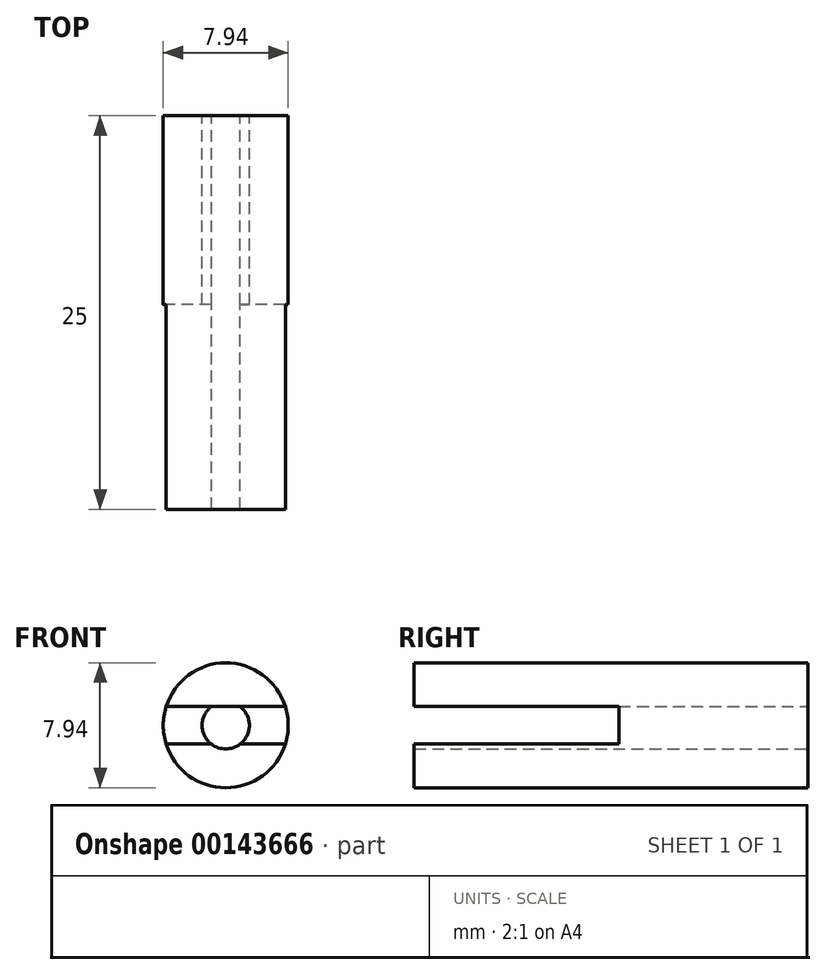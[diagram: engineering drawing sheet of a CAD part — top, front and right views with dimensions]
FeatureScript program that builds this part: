
annotation { "Feature Type Name" : "Feature", "Feature Type Description" : "" }
export const myFeature = defineFeature(function(context is Context, id is Id, definition is map)
    precondition{}
    {
        {
            var Q0;
            Q0=qCreatedBy(makeId("Front.planeOp"),FACE);
            var sketch = newSketch(context, id + "F0", { "sketchPlane" : qUnion([Q0])});
            skCircle(sketch, "E0", {"center": v(-45.73, 22.68) * mm, "radius": 3.97 * mm});
            skLineSegment(sketch, "E1", {"start": v(-41.94, 21.49) * mm, "end": v(-49.51, 21.49) * mm});
            skCircle(sketch, "E2", {"center": v(-45.73, 22.68) * mm, "radius": 1.5 * mm});
            skLineSegment(sketch, "E3", {"start": v(-41.94, 23.87) * mm, "end": v(-49.51, 23.87) * mm});
            skSolve(sketch);
        }
        {
            var Q0;
            Q0=makeQuery(id+"F0.imprint","IMPRINT",FACE,{"disambiguationData":[TD([[makeQuery(id+"F0.imprint","IMPRINT",EDGE,{"derivedFrom":sQuery(id+"F0.wireOp",EDGE,"Usm6nLvA-fHHg-3Ia8-UZyx-qVzBW3ukUWrC.bottom")}),-1.0]])]});
            var Q1;
            {var subQ0=sQuery(id+"F0.wireOp",EDGE,"E1");var subQ1=sQuery(id+"F0.wireOp",EDGE,"E0");var subQ2=makeQuery(id+"F0.imprint","INTERSECT",VERTEX,{"disambiguationData":[OD(0.0)],"derivedFrom":[subQ1,subQ0]});Q1=makeQuery(id+"F0.imprint","IMPRINT",FACE,{"disambiguationData":[TD([[makeQuery(id+"F0.imprint","IMPRINT",EDGE,{"disambiguationData":[TD([[subQ2,1.0]])],"derivedFrom":subQ1}),1.0]])]});}
            var Q2;
            {var subQ0=sQuery(id+"F0.wireOp",EDGE,"E2");var subQ1=sQuery(id+"F0.wireOp",EDGE,"E1");var subQ2=makeQuery(id+"F0.imprint","INTERSECT",VERTEX,{"disambiguationData":[OD(0.0)],"derivedFrom":[subQ1,subQ0]});Q2=makeQuery(id+"F0.imprint","IMPRINT",FACE,{"disambiguationData":[TD([[makeQuery(id+"F0.imprint","IMPRINT",EDGE,{"disambiguationData":[TD([[subQ2,-1.0]])],"derivedFrom":subQ1}),1.0]])]});}
            var Q3;
            {var subQ0=sQuery(id+"F0.wireOp",EDGE,"E3");var subQ1=sQuery(id+"F0.wireOp",EDGE,"E2");var subQ2=makeQuery(id+"F0.imprint","INTERSECT",VERTEX,{"disambiguationData":[OD(0.0)],"derivedFrom":[subQ1,subQ0]});Q3=makeQuery(id+"F0.imprint","IMPRINT",FACE,{"disambiguationData":[TD([[makeQuery(id+"F0.imprint","IMPRINT",EDGE,{"disambiguationData":[TD([[subQ2,1.0]])],"derivedFrom":subQ1}),1.0]])]});}
            var Q4;
            {var subQ0=sQuery(id+"F0.wireOp",EDGE,"E3");var subQ1=sQuery(id+"F0.wireOp",EDGE,"E0");var subQ2=makeQuery(id+"F0.imprint","INTERSECT",VERTEX,{"disambiguationData":[OD(0.0)],"derivedFrom":[subQ1,subQ0]});Q4=makeQuery(id+"F0.imprint","IMPRINT",FACE,{"disambiguationData":[TD([[makeQuery(id+"F0.imprint","IMPRINT",EDGE,{"disambiguationData":[TD([[subQ2,-1.0]])],"derivedFrom":subQ1}),1.0]])]});}
            extrude(context, id + "F1", {"entities" : qUnion([Q0, Q1, Q2, Q3, Q4]), "depth" : 25 * mm});
        }
        {
            var Q0;
            {var subQ0=sQuery(id+"F0.wireOp",EDGE,"E1");var subQ1=sQuery(id+"F0.wireOp",EDGE,"E0");var subQ2=makeQuery(id+"F0.imprint","INTERSECT",VERTEX,{"disambiguationData":[OD(1.0)],"derivedFrom":[subQ1,subQ0]});Q0=makeQuery(id+"F0.imprint","IMPRINT",FACE,{"disambiguationData":[TD([[makeQuery(id+"F0.imprint","IMPRINT",EDGE,{"disambiguationData":[TD([[subQ2,1.0]])],"derivedFrom":subQ1}),1.0]])]});}
            var Q1;
            {var subQ0=sQuery(id+"F0.wireOp",EDGE,"E1");var subQ1=sQuery(id+"F0.wireOp",EDGE,"E0");var subQ2=makeQuery(id+"F0.imprint","INTERSECT",VERTEX,{"disambiguationData":[OD(0.0)],"derivedFrom":[subQ1,subQ0]});Q1=makeQuery(id+"F0.imprint","IMPRINT",FACE,{"disambiguationData":[TD([[makeQuery(id+"F0.imprint","IMPRINT",EDGE,{"disambiguationData":[TD([[subQ2,-1.0]])],"derivedFrom":subQ1}),1.0]])]});}
            extrude(context, id + "F2", {"entities" : qUnion([Q0, Q1]), "operationType" : NewBodyOperationType.ADD, "depth" : 12 * mm});
        }
    });
